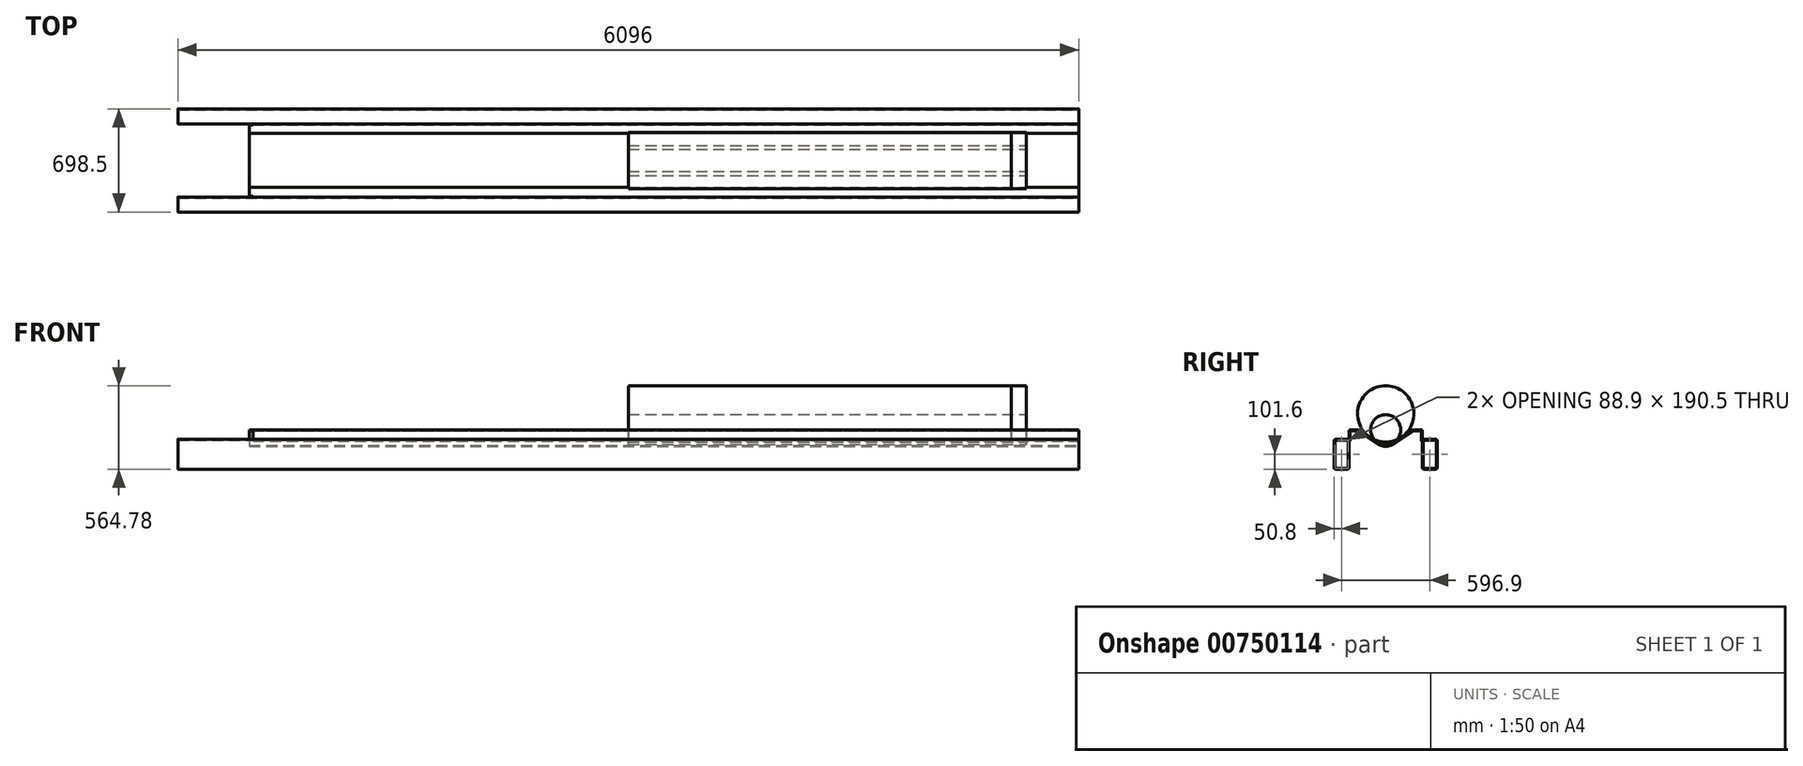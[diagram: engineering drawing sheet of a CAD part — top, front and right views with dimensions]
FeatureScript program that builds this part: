
annotation { "Feature Type Name" : "Feature", "Feature Type Description" : "" }
export const myFeature = defineFeature(function(context is Context, id is Id, definition is map)
    precondition{}
    {
        {
            var Q0;
            Q0=qCreatedBy(makeId("Right.planeOp"),FACE);
            var sketch = newSketch(context, id + "F0", { "sketchPlane" : qUnion([Q0])});
            skPoint(sketch, "E0", {"position": v(0, 0) * mm});
            skLineSegment(sketch, "E1", {"start": v(0, 200.93) * mm, "end": v(0, -305.7) * mm, "construction": true});
            skLineSegment(sketch, "E2.bottom", {"start": v(-336.55, 57.15) * mm, "end": v(-260.35, 57.15) * mm});
            skLineSegment(sketch, "E2.top", {"start": v(-336.55, -146.05) * mm, "end": v(-260.35, -146.05) * mm});
            skLineSegment(sketch, "E2.left", {"start": v(-349.25, 44.45) * mm, "end": v(-349.25, -133.35) * mm});
            skLineSegment(sketch, "E2.right", {"start": v(-247.65, 44.45) * mm, "end": v(-247.65, -133.35) * mm});
            skPoint(sketch, "E3.visualSharp", {"position": v(-247.65, 57.15) * mm});
            skArc(sketch, "E3.filletArc", {"start": v(-247.65, 44.45) * mm, "mid": v(-251.37, 53.43) * mm, "end": v(-260.35, 57.15) * mm});
            skPoint(sketch, "E4.visualSharp", {"position": v(-349.25, -146.05) * mm});
            skArc(sketch, "E4.filletArc", {"start": v(-349.25, -133.35) * mm, "mid": v(-345.53, -142.33) * mm, "end": v(-336.55, -146.05) * mm});
            skPoint(sketch, "E5.visualSharp", {"position": v(-247.65, -146.05) * mm});
            skArc(sketch, "E5.filletArc", {"start": v(-260.35, -146.05) * mm, "mid": v(-251.37, -142.33) * mm, "end": v(-247.65, -133.35) * mm});
            skPoint(sketch, "E6.visualSharp", {"position": v(-349.25, 57.15) * mm});
            skArc(sketch, "E6.filletArc", {"start": v(-336.55, 57.15) * mm, "mid": v(-345.53, 53.43) * mm, "end": v(-349.25, 44.45) * mm});
            skLineSegment(sketch, "E7.MirrorCS", {"start": v(247.65, 44.45) * mm, "end": v(247.65, -133.35) * mm});
            skArc(sketch, "E8.MirrorCS", {"start": v(247.65, 44.45) * mm, "mid": v(251.37, 53.43) * mm, "end": v(260.35, 57.15) * mm});
            skLineSegment(sketch, "E9.MirrorCS", {"start": v(336.55, 57.15) * mm, "end": v(260.35, 57.15) * mm});
            skArc(sketch, "E10.MirrorCS", {"start": v(336.55, 57.15) * mm, "mid": v(345.53, 53.43) * mm, "end": v(349.25, 44.45) * mm});
            skLineSegment(sketch, "E11.MirrorCS", {"start": v(349.25, 44.45) * mm, "end": v(349.25, -133.35) * mm});
            skArc(sketch, "E12.MirrorCS", {"start": v(349.25, -133.35) * mm, "mid": v(345.53, -142.33) * mm, "end": v(336.55, -146.05) * mm});
            skLineSegment(sketch, "E13.MirrorCS", {"start": v(336.55, -146.05) * mm, "end": v(260.35, -146.05) * mm});
            skPoint(sketch, "E14.MirrorP", {"position": v(247.65, -146.05) * mm});
            skArc(sketch, "E15.MirrorCS", {"start": v(260.35, -146.05) * mm, "mid": v(251.37, -142.33) * mm, "end": v(247.65, -133.35) * mm});
            skPoint(sketch, "E16.MirrorP", {"position": v(247.65, 57.15) * mm});
            skLineSegment(sketch, "E17", {"start": v(-182.86, 120.65) * mm, "end": v(-41.97, 27.69) * mm});
            skLineSegment(sketch, "E18.MirrorCS", {"start": v(182.86, 120.65) * mm, "end": v(41.97, 27.69) * mm});
            skLineSegment(sketch, "E19", {"start": v(-227.24, 120.65) * mm, "end": v(0, 120.65) * mm, "construction": true});
            skCircle(sketch, "E20", {"center": v(0, 228.23) * mm, "radius": 190.5 * mm});
            skArc(sketch, "E21.filletArc", {"start": v(-41.97, 27.69) * mm, "mid": v(0, 15.1) * mm, "end": v(41.97, 27.69) * mm});
            skCircle(sketch, "E22", {"center": v(0, 121.72) * mm, "radius": 101.6 * mm});
            skCircle(sketch, "E23", {"center": v(0, 67.4) * mm, "radius": 50.8 * mm, "construction": true});
            skArc(sketch, "E24.0", {"start": v(-336.55, 50.8) * mm, "mid": v(-341.04, 48.94) * mm, "end": v(-342.9, 44.45) * mm});
            skLineSegment(sketch, "E24.1", {"start": v(-342.9, 44.45) * mm, "end": v(-342.9, -133.35) * mm});
            skLineSegment(sketch, "E24.2", {"start": v(-336.55, 50.8) * mm, "end": v(-260.35, 50.8) * mm});
            skArc(sketch, "E24.3", {"start": v(-342.9, -133.35) * mm, "mid": v(-341.04, -137.84) * mm, "end": v(-336.55, -139.7) * mm});
            skArc(sketch, "E24.4", {"start": v(-254, 44.45) * mm, "mid": v(-255.86, 48.94) * mm, "end": v(-260.35, 50.8) * mm});
            skLineSegment(sketch, "E24.5", {"start": v(-254, 44.45) * mm, "end": v(-254, -133.35) * mm});
            skArc(sketch, "E24.6", {"start": v(-260.35, -139.7) * mm, "mid": v(-255.86, -137.84) * mm, "end": v(-254, -133.35) * mm});
            skLineSegment(sketch, "E24.7", {"start": v(-336.55, -139.7) * mm, "end": v(-260.35, -139.7) * mm});
            skArc(sketch, "E25.0", {"start": v(336.55, 50.8) * mm, "mid": v(341.04, 48.94) * mm, "end": v(342.9, 44.45) * mm});
            skLineSegment(sketch, "E25.1", {"start": v(342.9, 44.45) * mm, "end": v(342.9, -133.35) * mm});
            skLineSegment(sketch, "E25.2", {"start": v(336.55, 50.8) * mm, "end": v(260.35, 50.8) * mm});
            skArc(sketch, "E25.3", {"start": v(342.9, -133.35) * mm, "mid": v(341.04, -137.84) * mm, "end": v(336.55, -139.7) * mm});
            skArc(sketch, "E25.4", {"start": v(254, 44.45) * mm, "mid": v(255.86, 48.94) * mm, "end": v(260.35, 50.8) * mm});
            skLineSegment(sketch, "E25.5", {"start": v(254, 44.45) * mm, "end": v(254, -133.35) * mm});
            skArc(sketch, "E25.6", {"start": v(260.35, -139.7) * mm, "mid": v(255.86, -137.84) * mm, "end": v(254, -133.35) * mm});
            skLineSegment(sketch, "E25.7", {"start": v(336.55, -139.7) * mm, "end": v(260.35, -139.7) * mm});
            skLineSegment(sketch, "E26", {"start": v(-278.75, 57.15) * mm, "end": v(-269.35, 57.15) * mm});
            skLineSegment(sketch, "E27", {"start": v(-278.75, 57.15) * mm, "end": v(-268.14, 57.15) * mm});
            skLineSegment(sketch, "E28", {"start": v(-182.86, 120.65) * mm, "end": v(-247.65, 120.65) * mm});
            skLineSegment(sketch, "E29", {"start": v(-247.65, 120.65) * mm, "end": v(-247.65, 44.45) * mm});
            skLineSegment(sketch, "E30", {"start": v(247.65, 44.45) * mm, "end": v(247.65, 120.65) * mm});
            skLineSegment(sketch, "E31", {"start": v(247.65, 120.65) * mm, "end": v(182.86, 120.65) * mm});
            skLineSegment(sketch, "E32.0", {"start": v(-241.3, 114.3) * mm, "end": v(-241.3, 44.45) * mm});
            skLineSegment(sketch, "E32.1", {"start": v(-184.77, 114.3) * mm, "end": v(-241.3, 114.3) * mm});
            skLineSegment(sketch, "E32.2", {"start": v(-184.77, 114.3) * mm, "end": v(-45.46, 22.39) * mm});
            skLineSegment(sketch, "E32.3", {"start": v(241.3, 44.45) * mm, "end": v(241.3, 114.3) * mm});
            skLineSegment(sketch, "E32.4", {"start": v(241.3, 114.3) * mm, "end": v(184.77, 114.3) * mm});
            skLineSegment(sketch, "E32.5", {"start": v(184.77, 114.3) * mm, "end": v(45.46, 22.39) * mm});
            skArc(sketch, "E32.6", {"start": v(-45.46, 22.39) * mm, "mid": v(0, 8.74) * mm, "end": v(45.46, 22.39) * mm});
            skLineSegment(sketch, "E33", {"start": v(247.65, 44.45) * mm, "end": v(241.3, 44.45) * mm});
            skLineSegment(sketch, "E34", {"start": v(-241.3, 44.45) * mm, "end": v(-247.65, 44.45) * mm});
            skSolve(sketch);
        }
        {
            var Q0;
            Q0=makeQuery(id+"F0.imprint","IMPRINT",FACE,{"disambiguationData":[TD([[makeQuery(id+"F0.imprint","IMPRINT",EDGE,{"derivedFrom":sQuery(id+"F0.wireOp",EDGE,"E2.top")}),1.0]])]});
            var Q1;
            Q1=makeQuery(id+"F0.imprint","IMPRINT",FACE,{"disambiguationData":[TD([[makeQuery(id+"F0.imprint","IMPRINT",EDGE,{"derivedFrom":sQuery(id+"F0.wireOp",EDGE,"E7.MirrorCS")}),1.0]])]});
            extrude(context, id + "F1", {"entities" : qUnion([Q0, Q1]), "oppositeDirection" : true, "depth" : 6096 * mm, "offsetDistance" : 25.4 * mm});
        }
        {
            var Q0;
            Q0=makeQuery(id+"F0.imprint","IMPRINT",FACE,{"disambiguationData":[TD([[makeQuery(id+"F0.imprint","IMPRINT",EDGE,{"derivedFrom":sQuery(id+"F0.wireOp",EDGE,"E17")}),-1.0]])]});
            var Q1;
            {var subQ4=sQuery(id+"F0.wireOp",EDGE,"40Ta9XpO-4Bih-OJ3X-wqKm-lZXZA3K83W1n");Q1=makeQuery(id+"F0.imprint","IMPRINT",FACE,{"disambiguationData":[TD([[makeQuery(id+"F0.imprint","IMPRINT",EDGE,{"derivedFrom":subQ4}),1.0]])]});}
            var Q2;
            {var subQ0=sQuery(id+"F0.wireOp",EDGE,"hLX8c9pQ-herN-AtC7-Xv8B-rJKkOfKo46Fv");Q2=makeQuery(id+"F0.imprint","IMPRINT",FACE,{"disambiguationData":[TD([[makeQuery(id+"F0.imprint","IMPRINT",EDGE,{"derivedFrom":subQ0}),-1.0]])]});}
            extrude(context, id + "F2", {"entities" : qUnion([Q0, Q1, Q2]), "oppositeDirection" : true, "depth" : 5588 * mm, "offsetDistance" : 25.4 * mm});
        }
        {
            var Q0;
            {var subQ0=sQuery(id+"F0.wireOp",EDGE,"E22");var subQ1=makeQuery(id+"F0.imprint","INTERSECT",VERTEX,{"derivedFrom":[sQuery(id+"F0.wireOp",EDGE,"E17"),subQ0]});Q0=makeQuery(id+"F0.imprint","IMPRINT",FACE,{"disambiguationData":[TD([[makeQuery(id+"F0.imprint","IMPRINT",EDGE,{"disambiguationData":[TD([[subQ1,-1.0]])],"derivedFrom":subQ0}),1.0]])]});}
            var Q1;
            {var subQ0=sQuery(id+"F0.wireOp",EDGE,"E22");var subQ1=sQuery(id+"F0.wireOp",EDGE,"E20");var subQ2=makeQuery(id+"F0.imprint","INTERSECT",VERTEX,{"disambiguationData":[OD(0.0)],"derivedFrom":[subQ1,subQ0]});Q1=makeQuery(id+"F0.imprint","IMPRINT",FACE,{"disambiguationData":[TD([[makeQuery(id+"F0.imprint","IMPRINT",EDGE,{"disambiguationData":[TD([[subQ2,-1.0]])],"derivedFrom":subQ1}),1.0]])]});}
            extrude(context, id + "F3", {"entities" : qUnion([Q0, Q1]), "oppositeDirection" : true, "depth" : 3048 * mm, "offsetDistance" : 25.4 * mm, "hasSecondDirection" : true, "secondDirectionOppositeDirection" : true, "secondDirectionDepth" : 355.6 * mm});
        }
        {
            var Q0;
            {var subQ0=sQuery(id+"F0.wireOp",EDGE,"E20");var subQ1=makeQuery(id+"F0.imprint","INTERSECT",VERTEX,{"derivedFrom":[sQuery(id+"F0.wireOp",EDGE,"E17"),subQ0]});Q0=makeQuery(id+"F0.imprint","IMPRINT",FACE,{"disambiguationData":[TD([[makeQuery(id+"F0.imprint","IMPRINT",EDGE,{"disambiguationData":[TD([[subQ1,-1.0]])],"derivedFrom":subQ0}),1.0]])]});}
            var Q1;
            {var subQ0=sQuery(id+"F0.wireOp",EDGE,"E22");var subQ1=sQuery(id+"F0.wireOp",EDGE,"E20");var subQ2=makeQuery(id+"F0.imprint","INTERSECT",VERTEX,{"disambiguationData":[OD(0.0)],"derivedFrom":[subQ1,subQ0]});Q1=makeQuery(id+"F0.imprint","IMPRINT",FACE,{"disambiguationData":[TD([[makeQuery(id+"F0.imprint","IMPRINT",EDGE,{"disambiguationData":[TD([[subQ2,-1.0]])],"derivedFrom":subQ1}),1.0]])]});}
            extrude(context, id + "F4", {"entities" : qUnion([Q0, Q1]), "oppositeDirection" : true, "depth" : 3048 * mm, "offsetDistance" : 25.4 * mm, "hasSecondDirection" : true, "secondDirectionOppositeDirection" : true, "secondDirectionDepth" : 457.2 * mm});
        }
        {
            var Q0;
            Q0=qCreatedBy(makeId("Right.planeOp"),FACE);
            cPlane(context, id + "F5", {"entities" : qUnion([Q0]), "cplaneType" : CPlaneType.OFFSET, "offset" : 6985 * mm, "oppositeDirection" : true, "width" : 152.4 * mm, "height" : 152.4 * mm});
        }
        {
            var Q0;
            Q0=makeQuery(id+"F2.opExtrude","CAP_FACE",FACE,{"disambiguationData":[OSD([sQuery(id+"F0.wireOp",EDGE,"E17"),sQuery(id+"F0.wireOp",EDGE,"E18.MirrorCS"),sQuery(id+"F0.wireOp",EDGE,"E21.filletArc"),sQuery(id+"F0.wireOp",EDGE,"E28"),sQuery(id+"F0.wireOp",EDGE,"E29"),sQuery(id+"F0.wireOp",EDGE,"E30"),sQuery(id+"F0.wireOp",EDGE,"E31"),sQuery(id+"F0.wireOp",EDGE,"E32.0"),sQuery(id+"F0.wireOp",EDGE,"E32.1"),sQuery(id+"F0.wireOp",EDGE,"E32.2"),sQuery(id+"F0.wireOp",EDGE,"E32.3"),sQuery(id+"F0.wireOp",EDGE,"E32.4"),sQuery(id+"F0.wireOp",EDGE,"E32.5"),sQuery(id+"F0.wireOp",EDGE,"E32.6"),sQuery(id+"F0.wireOp",EDGE,"E33"),sQuery(id+"F0.wireOp",EDGE,"E34")])],"isStart":false});
            var sketch = newSketch(context, id + "F6", { "sketchPlane" : qUnion([Q0])});
            skLineSegment(sketch, "E35.0", {"start": v(-241.3, 114.3) * mm, "end": v(-184.77, 114.3) * mm});
            skLineSegment(sketch, "E36.0", {"start": v(-184.77, 114.3) * mm, "end": v(-45.46, 22.39) * mm});
            skArc(sketch, "E37.0", {"start": v(45.46, 22.39) * mm, "mid": v(0, 8.74) * mm, "end": v(-45.46, 22.39) * mm});
            skLineSegment(sketch, "E38.0", {"start": v(184.77, 114.3) * mm, "end": v(45.46, 22.39) * mm});
            skLineSegment(sketch, "E39.0", {"start": v(184.77, 114.3) * mm, "end": v(241.3, 114.3) * mm});
            skLineSegment(sketch, "E40.0", {"start": v(182.86, 120.65) * mm, "end": v(241.3, 120.65) * mm});
            skLineSegment(sketch, "E41.0", {"start": v(182.86, 120.65) * mm, "end": v(41.97, 27.69) * mm});
            skArc(sketch, "E42.0", {"start": v(41.97, 27.69) * mm, "mid": v(0, 15.1) * mm, "end": v(-41.97, 27.69) * mm});
            skLineSegment(sketch, "E43.0", {"start": v(-182.86, 120.65) * mm, "end": v(-41.97, 27.69) * mm});
            skLineSegment(sketch, "E44.0", {"start": v(-241.3, 120.65) * mm, "end": v(-182.86, 120.65) * mm});
            skLineSegment(sketch, "E45", {"start": v(-241.3, 114.3) * mm, "end": v(-241.3, 120.65) * mm});
            skLineSegment(sketch, "E46", {"start": v(241.3, 114.3) * mm, "end": v(241.3, 120.65) * mm});
            skPoint(sketch, "E47.orphan", {"position": v(247.65, 120.65) * mm});
            skPoint(sketch, "E48.orphan", {"position": v(-247.65, 120.65) * mm});
            skSolve(sketch);
        }
        {
            var Q0;
            Q0=makeQuery(id+"F6.imprint","IMPRINT",FACE,{"disambiguationData":[TD([[makeQuery(id+"F6.imprint","IMPRINT",EDGE,{"derivedFrom":sQuery(id+"F6.wireOp",EDGE,"E35.0")}),1.0]])]});
            extrude(context, id + "F7", {"entities" : qUnion([Q0]), "operationType" : NewBodyOperationType.ADD, "depth" : 25.4 * mm, "offsetDistance" : 25.4 * mm});
        }
    });
